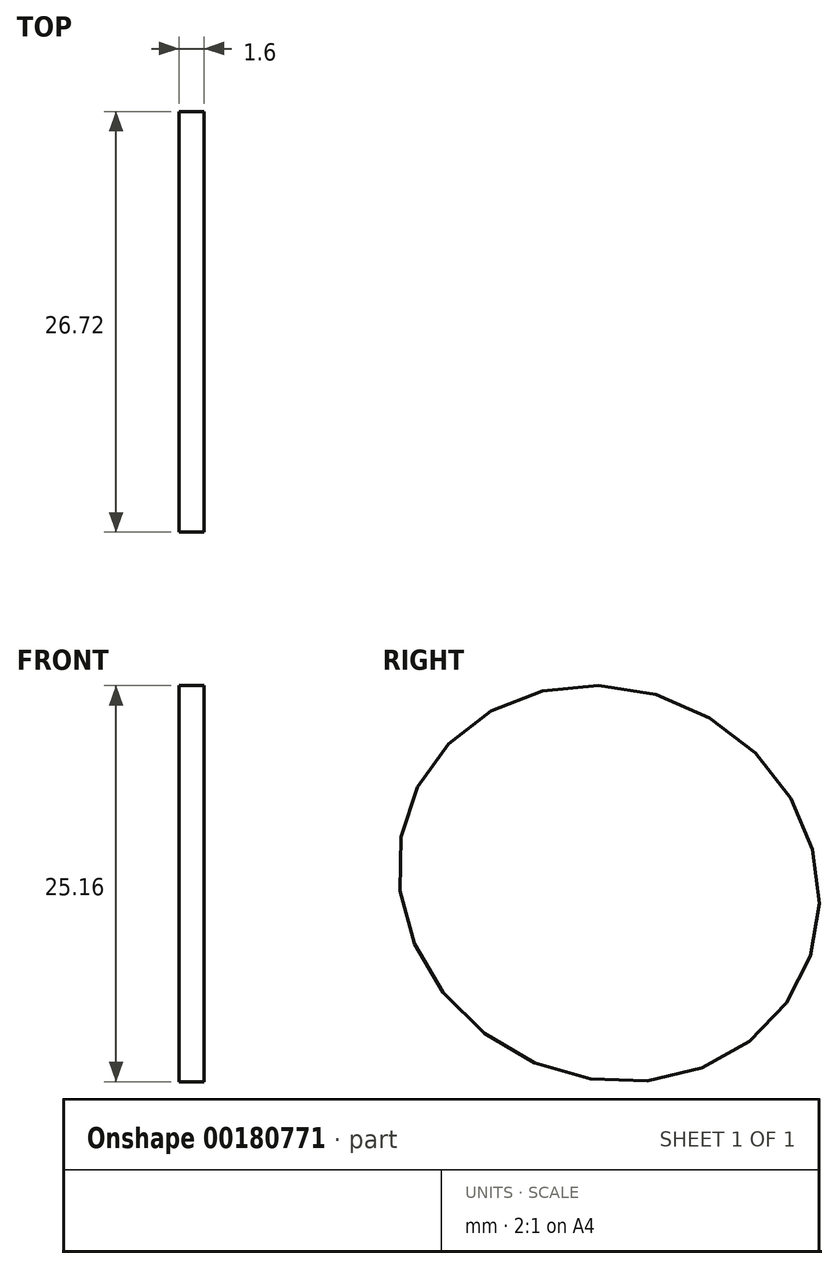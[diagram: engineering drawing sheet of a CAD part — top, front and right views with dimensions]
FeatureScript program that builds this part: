
annotation { "Feature Type Name" : "Feature", "Feature Type Description" : "" }
export const myFeature = defineFeature(function(context is Context, id is Id, definition is map)
    precondition{}
    {
        {
            var Q0;
            Q0=qCreatedBy(makeId("Right.planeOp"),FACE);
            var sketch = newSketch(context, id + "F0", { "sketchPlane" : qUnion([Q0])});
            skEllipse(sketch, "E0", {"center": v(0, 0) * mm, "majorRadius": 13.61 * mm, "minorRadius": 12.3 * mm, "majorAxis": v(-0.9, 0.45)});
            skSolve(sketch);
        }
        {
            var Q0;
            Q0 = qSketchRegion(id + "F0", true);
            extrude(context, id + "F1", {"entities" : qUnion([Q0]), "endBound" : BoundingType.SYMMETRIC, "depth" : 1.6 * mm});
        }
    });
